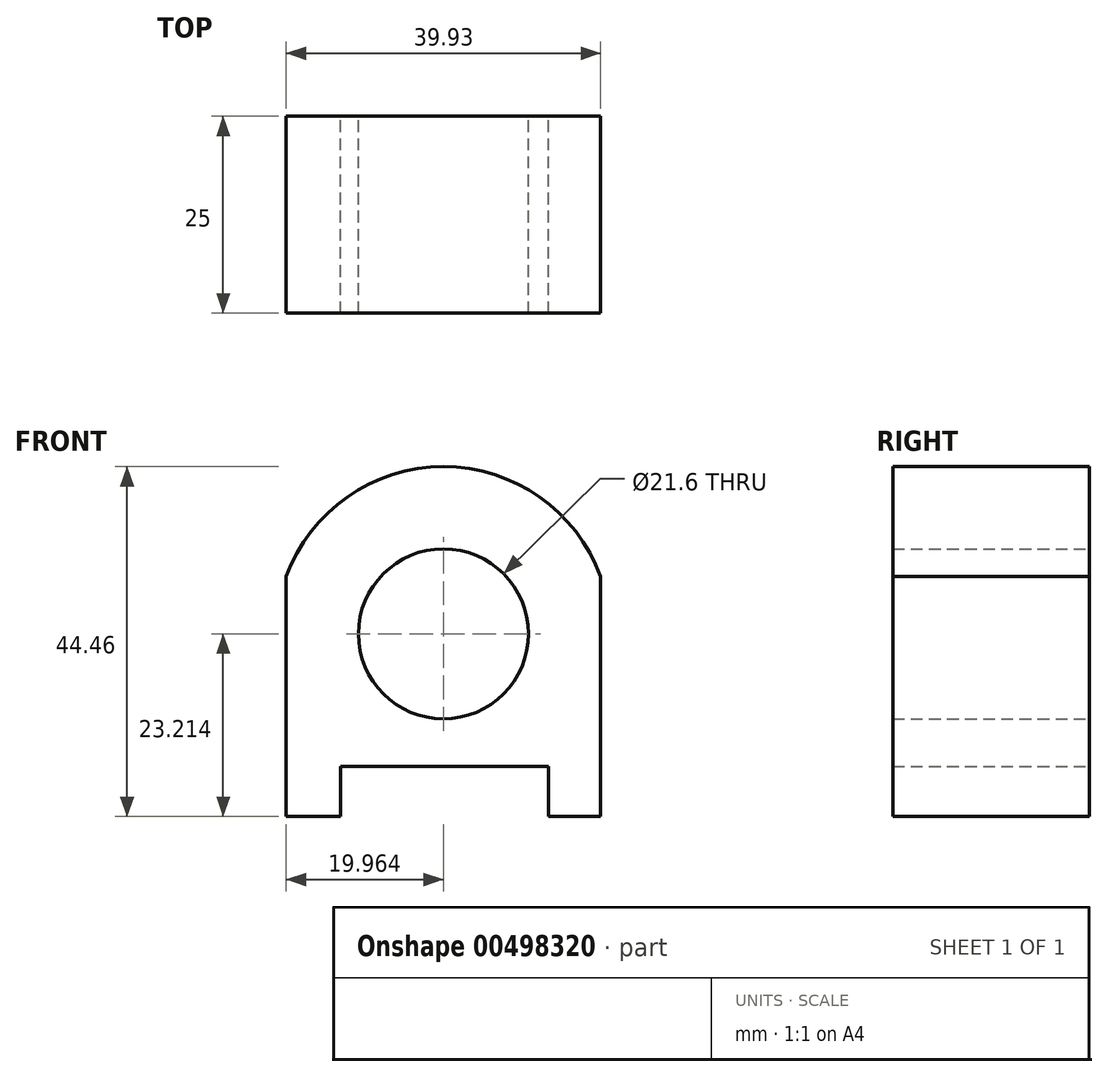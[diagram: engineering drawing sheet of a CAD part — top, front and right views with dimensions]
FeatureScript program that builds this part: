
annotation { "Feature Type Name" : "Feature", "Feature Type Description" : "" }
export const myFeature = defineFeature(function(context is Context, id is Id, definition is map)
    precondition{}
    {
        {
            var Q0;
            Q0=qCreatedBy(makeId("Front.planeOp"),FACE);
            var sketch = newSketch(context, id + "F0", { "sketchPlane" : qUnion([Q0])});
            skLineSegment(sketch, "E0", {"start": v(0, 0) * mm, "end": v(-6.6, 0) * mm});
            skLineSegment(sketch, "E1", {"start": v(-6.6, 0) * mm, "end": v(-6.6, 6.37) * mm});
            skLineSegment(sketch, "E2", {"start": v(-6.6, 6.37) * mm, "end": v(-33.02, 6.37) * mm});
            skLineSegment(sketch, "E3", {"start": v(-33.02, 6.37) * mm, "end": v(-33.02, 0) * mm});
            skLineSegment(sketch, "E4", {"start": v(-33.02, 0) * mm, "end": v(-39.93, 0) * mm});
            skLineSegment(sketch, "E5", {"start": v(-39.93, 0) * mm, "end": v(-39.93, 30.49) * mm});
            skLineSegment(sketch, "E6", {"start": v(0, 30.49) * mm, "end": v(0, 0) * mm});
            skArc(sketch, "E7", {"start": v(0, 30.49) * mm, "mid": v(-19.97, 44.46) * mm, "end": v(-39.93, 30.49) * mm});
            skCircle(sketch, "E8", {"center": v(-19.97, 23.21) * mm, "radius": 10.8 * mm});
            skSolve(sketch);
        }
        {
            var Q0;
            Q0=makeQuery(id+"F0.imprint","IMPRINT",FACE,{"disambiguationData":[TD([[makeQuery(id+"F0.imprint","IMPRINT",EDGE,{"derivedFrom":sQuery(id+"F0.wireOp",EDGE,"E0")}),-1.0]])]});
            extrude(context, id + "F1", {"entities" : qUnion([Q0]), "depth" : 25 * mm});
        }
    });
